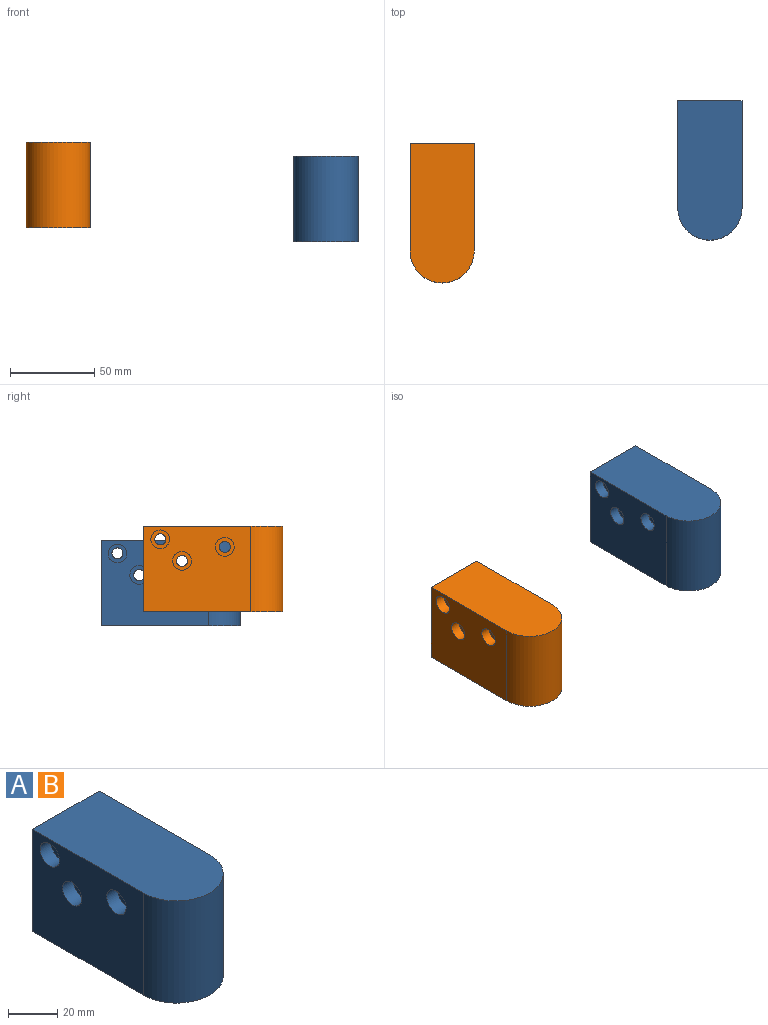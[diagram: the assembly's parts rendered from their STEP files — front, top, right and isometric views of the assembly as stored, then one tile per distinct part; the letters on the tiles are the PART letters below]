
ASSEMBLY  parts=2 mates=1
PART A: 15 faces, bbox 38.1x82.6x50.8 mm
  f0: plane 63.5x50.8mm, normal (-1,0,0), area 2934.8mm2, adj f1,f3,f4,f5,f8,f11,f14
  f1: cylinder r=19.05mm len=50.8mm, axis (0,0,-1), area 3040.2mm2, adj f0,f2,f4,f5
  f2: plane 63.5x50.8mm, normal (1,0,0), area 3125.4mm2, adj f1,f3,f4,f5,f6,f9,f12
  f3: plane 50.8x38.1mm, normal (0,1,0), area 1935.5mm2, adj f0,f2,f4,f5
  f4: plane 82.55x38.1mm, normal (0,0,1), area 2989.4mm2, adj f0,f1,f2,f3
  f5: plane 82.55x38.1mm, normal (0,0,-1), area 2989.4mm2, adj f0,f1,f2,f3
  f6: cylinder r=3.26mm len=31.75mm, axis (-1,0,0), area 651.1mm2, adj f2,f7
  f7: plane 11.11x11.11mm, normal (-1,0,0), area 63.5mm2, adj f6,f8
  f8: cylinder r=5.56mm len=11.11mm, axis (-1,0,0), area 221.7mm2, adj f0,f7
  f9: cylinder r=3.26mm len=31.75mm, axis (-1,0,0), area 651.1mm2, adj f2,f10
  f10: plane 11.11x11.11mm, normal (-1,0,0), area 63.5mm2, adj f9,f11
  f11: cylinder r=5.56mm len=11.11mm, axis (-1,0,0), area 221.7mm2, adj f0,f10
  f12: cylinder r=3.26mm len=31.75mm, axis (-1,0,0), area 651.1mm2, adj f2,f13
  f13: plane 11.11x11.11mm, normal (-1,0,0), area 63.5mm2, adj f12,f14
  f14: cylinder r=5.56mm len=11.11mm, axis (-1,0,0), area 221.7mm2, adj f0,f13
PART B: same geometry as A
PLACE A t=(202.81,23.12,-129.73)mm
PLACE B t=(43.97,-2.27,-121.4)mm
MATE parallel B.f2 <-> A.f0  axis (1,0,0) through (82.07,29.33,-96.37)mm
